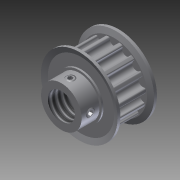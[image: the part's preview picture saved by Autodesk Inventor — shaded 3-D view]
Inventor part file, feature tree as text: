
AUTODESK INVENTOR PART (.ipt)
format: ipt  version: 2012 (Build 160160000, 160)  size: 320,000 bytes
history: native  units: in
note: dims shown in document units (in); Inventor stores cm internally (conversion verified against a paired STEP export)
features: sketch x2, extrude x1, thread x1, imported_body x1, projected_geometry x1
ambient origin geometry x8: Origin, YZ Plane, XZ Plane, XY Plane, X Axis, Y Axis, Z Axis, Center Point
feature tree (6):
  sketch  "Sketch1"  dims[d0=0.375in d1=3.937in d2=0.0in d10=0.2106in]
  extrude  "Extrusion1"  Depth=3.937in TaperAngle=0.0deg
  sketch  "Sketch3"  dims[d11=0.0787in d12=0.0787in d14=0.0394in d17=0.3937in d18=0.0in]
  thread  "Thread1"  [1 undecoded]
  imported_body  "Base1"
  projected_geometry  "Projected Loop1"
note: 1 required parameter value undecoded (feature->parameter linkage not recoverable at this tier; creation-order binding heuristic only, values carry confidence <= 0.55)
